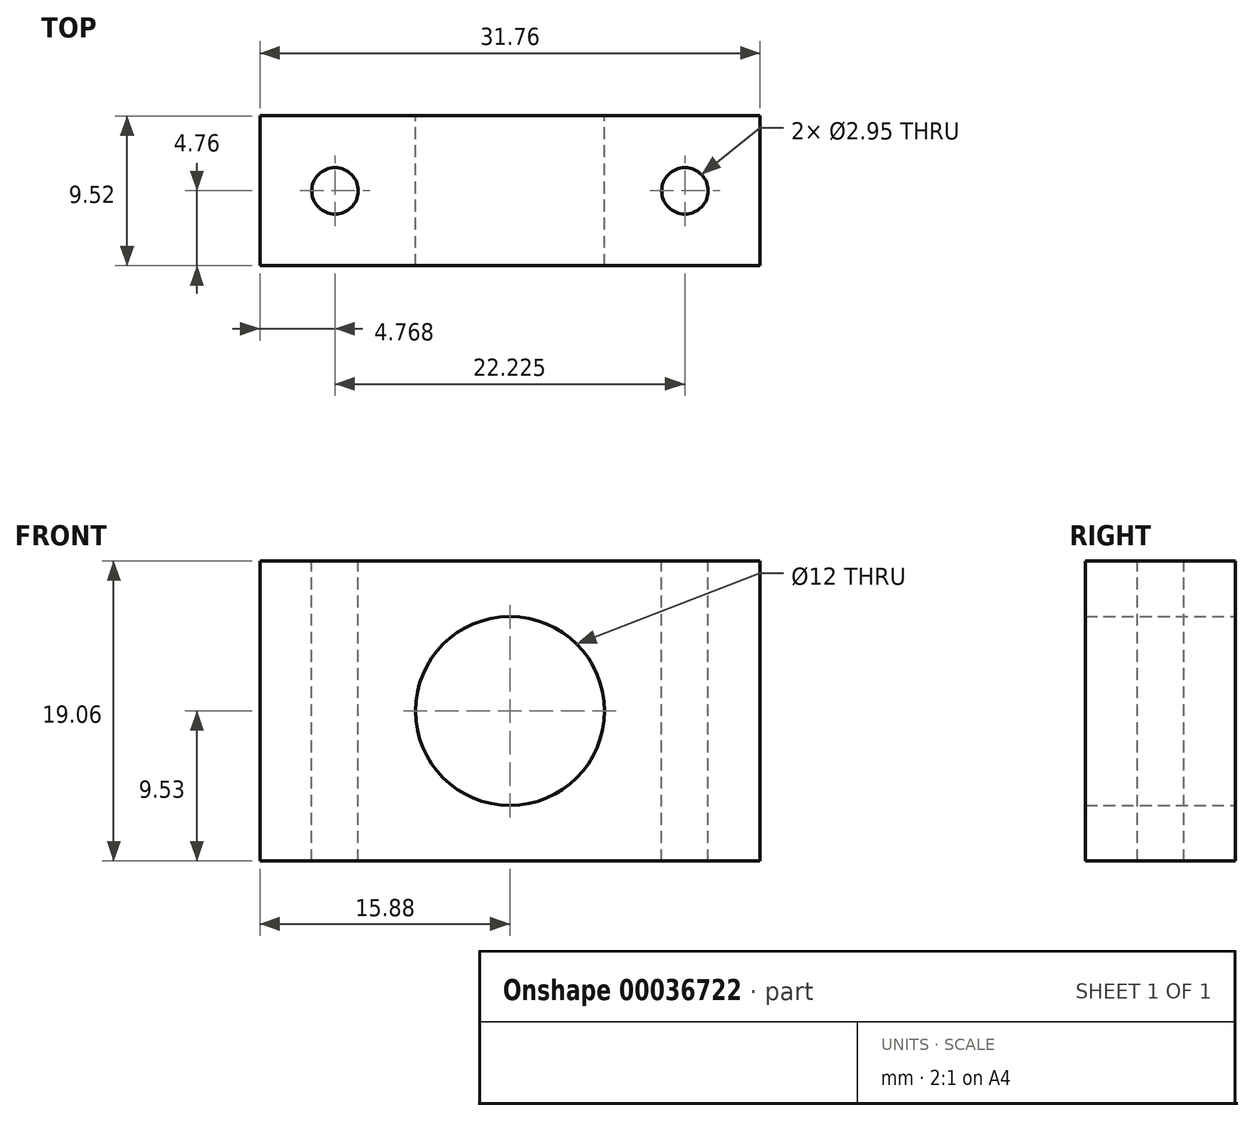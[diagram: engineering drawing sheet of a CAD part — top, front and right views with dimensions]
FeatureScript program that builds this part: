
annotation { "Feature Type Name" : "Feature", "Feature Type Description" : "" }
export const myFeature = defineFeature(function(context is Context, id is Id, definition is map)
    precondition{}
    {
        {
            var Q0;
            Q0=qCreatedBy(makeId("Front.planeOp"),FACE);
            var sketch = newSketch(context, id + "F0", { "sketchPlane" : qUnion([Q0])});
            skCircle(sketch, "E0", {"center": v(0, 0) * mm, "radius": 6 * mm});
            skLineSegment(sketch, "E1.bottom", {"start": v(15.88, 9.53) * mm, "end": v(-15.88, 9.53) * mm});
            skLineSegment(sketch, "E1.top", {"start": v(15.87, -9.53) * mm, "end": v(-15.88, -9.53) * mm});
            skLineSegment(sketch, "E1.left", {"start": v(15.88, 9.53) * mm, "end": v(15.87, -9.53) * mm});
            skLineSegment(sketch, "E1.right", {"start": v(-15.87, 9.53) * mm, "end": v(-15.88, -9.53) * mm});
            skSolve(sketch);
        }
        {
            var Q0;
            Q0=makeQuery(id+"F0.imprint","IMPRINT",FACE,{"disambiguationData":[TD([[makeQuery(id+"F0.imprint","IMPRINT",EDGE,{"derivedFrom":sQuery(id+"F0.wireOp",EDGE,"E0")}),-1.0]])]});
            extrude(context, id + "F1", {"entities" : qUnion([Q0]), "endBound" : BoundingType.SYMMETRIC, "depth" : 9.52 * mm, "offsetDistance" : 25.4 * mm});
        }
        {
            var Q0;
            Q0=makeQuery(id+"F1.opExtrude","SWEPT_FACE",FACE,{"disambiguationData":[OSD([sQuery(id+"F0.wireOp",EDGE,"E1.bottom")])]});
            var sketch = newSketch(context, id + "F2", { "sketchPlane" : qUnion([Q0])});
            skPoint(sketch, "E2", {"position": v(-11.11, 0) * mm});
            skPoint(sketch, "E3", {"position": v(11.11, 0) * mm});
            skSolve(sketch);
        }
        {
            var Q0;
            Q0=sQuery(id+"F2.wireOp",VERTEX,"E2");
            var Q1;
            Q1=sQuery(id+"F2.wireOp",VERTEX,"E3");
            var Q2;
            Q2=makeQuery(id+"F1.opExtrude","SWEPT_BODY",BODY,{"disambiguationData":[OSD([sQuery(id+"F0.wireOp",EDGE,"E0"),sQuery(id+"F0.wireOp",EDGE,"E1.bottom"),sQuery(id+"F0.wireOp",EDGE,"E1.top"),sQuery(id+"F0.wireOp",EDGE,"E1.left"),sQuery(id+"F0.wireOp",EDGE,"E1.right")])]});
            hole(context, id + "F3", {"style" : HoleStyle.SIMPLE, "endStyle" : HoleEndStyle.THROUGH, "standardTappedOrClearance" : lookupTablePath({ "standard" : "ANSI", "fit" : "Close", "size" : "#4", "type" : "Clearance" }), "standardBlindInLast" : lookupTablePath({ "fit" : "Close", "standard" : "ANSI", "size" : "#4", "type" : "Clearance" }), "holeDiameter" : 2.95 * mm, "majorDiameter" : 6.35 * mm, "tappedDepth" : 6.35 * mm, "tapClearance" : 3, "locations" : qUnion([Q0, Q1]), "scope" : qUnion([Q2])});
        }
    });
